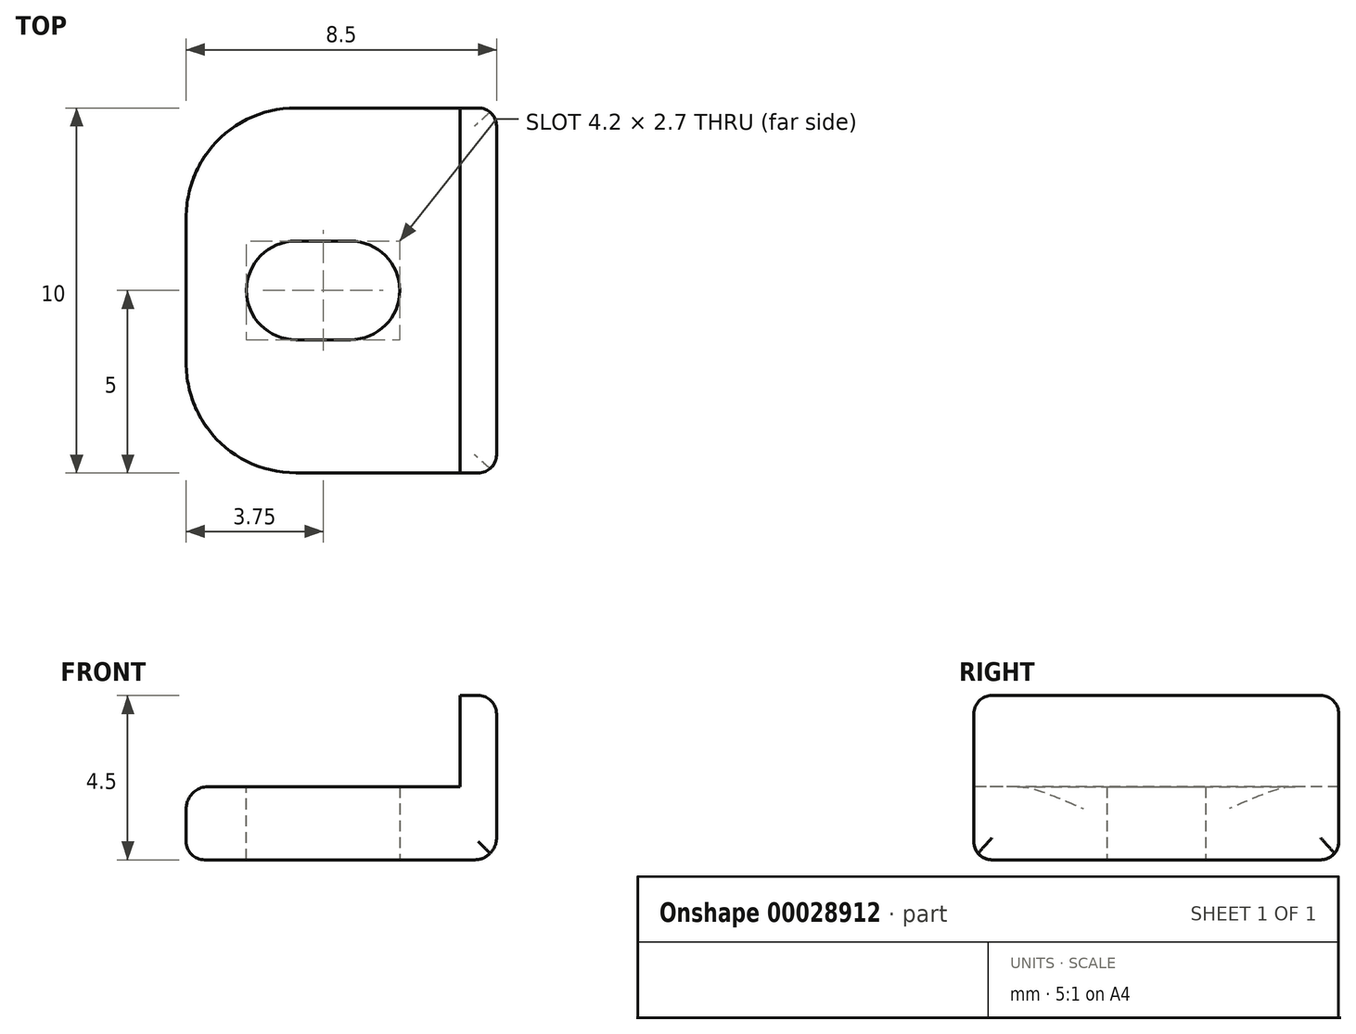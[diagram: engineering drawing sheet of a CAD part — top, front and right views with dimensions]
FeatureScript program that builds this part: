
annotation { "Feature Type Name" : "Feature", "Feature Type Description" : "" }
export const myFeature = defineFeature(function(context is Context, id is Id, definition is map)
    precondition{}
    {
        {
            var Q0;
            Q0=qCreatedBy(makeId("Top.planeOp"),FACE);
            var sketch = newSketch(context, id + "F0", { "sketchPlane" : qUnion([Q0])});
            skLineSegment(sketch, "E0.bottom", {"start": v(0, -10) * mm, "end": v(8.5, -10) * mm});
            skLineSegment(sketch, "E0.top", {"start": v(0, 0) * mm, "end": v(8.5, 0) * mm});
            skLineSegment(sketch, "E0.left", {"start": v(0, -10) * mm, "end": v(0, 0) * mm});
            skLineSegment(sketch, "E0.right", {"start": v(8.5, -10) * mm, "end": v(8.5, 0) * mm});
            skPoint(sketch, "E1", {"position": v(0, -5) * mm});
            skLineSegment(sketch, "E2", {"start": v(7.5, 0) * mm, "end": v(7.5, -10) * mm, "construction": true});
            skLineSegment(sketch, "E3", {"start": v(0, -5) * mm, "end": v(7.5, -5) * mm, "construction": true});
            skLineSegment(sketch, "E4.rect.bottom", {"start": v(5.85, -3.65) * mm, "end": v(1.65, -3.65) * mm});
            skLineSegment(sketch, "E4.rect.top", {"start": v(5.85, -6.35) * mm, "end": v(1.65, -6.35) * mm});
            skLineSegment(sketch, "E4.rect.left", {"start": v(5.85, -3.65) * mm, "end": v(5.85, -6.35) * mm});
            skLineSegment(sketch, "E4.rect.right", {"start": v(1.65, -3.65) * mm, "end": v(1.65, -6.35) * mm});
            skPoint(sketch, "E4.rect.middle", {"position": v(3.75, -5) * mm});
            skSolve(sketch);
        }
        {
            var Q0;
            Q0=makeQuery(id+"F0.imprint","IMPRINT",FACE,{"disambiguationData":[TD([[makeQuery(id+"F0.imprint","IMPRINT",EDGE,{"derivedFrom":sQuery(id+"F0.wireOp",EDGE,"E0.bottom")}),1.0]])]});
            extrude(context, id + "F1", {"entities" : qUnion([Q0]), "depth" : 2 * mm});
        }
        {
            var Q0;
            Q0=makeQuery(id+"F1.opExtrude","CAP_FACE",FACE,{"disambiguationData":[OSD([sQuery(id+"F0.wireOp",EDGE,"E0.bottom"),sQuery(id+"F0.wireOp",EDGE,"E0.top"),sQuery(id+"F0.wireOp",EDGE,"E0.left"),sQuery(id+"F0.wireOp",EDGE,"E0.right"),sQuery(id+"F0.wireOp",EDGE,"ae051ecd-3f90-4b7e-8cea-5822f81e962c")])],"isStart":false});
            var sketch = newSketch(context, id + "F2", { "sketchPlane" : qUnion([Q0])});
            skLineSegment(sketch, "E5", {"start": v(7.5, 0) * mm, "end": v(7.5, -10) * mm});
            skSolve(sketch);
        }
        {
            var Q0;
            {var subQ1=sQuery(id+"F2.wireOp",EDGE,"E5");Q0=makeQuery(id+"F2.imprint","IMPRINT",FACE,{"disambiguationData":[TD([[makeQuery(id+"F2.imprint","IMPRINT",EDGE,{"derivedFrom":subQ1}),1.0]])]});}
            extrude(context, id + "F3", {"entities" : qUnion([Q0]), "operationType" : NewBodyOperationType.ADD, "depth" : 2.5 * mm});
        }
        {
            var Q0;
            Q0=makeQuery(id+"F1.opExtrude","CAP_EDGE",EDGE,{"disambiguationData":[OSD([sQuery(id+"F0.wireOp",EDGE,"E0.bottom")])],"isStart":true});
            var Q1;
            {var subQ0=sQuery(id+"F0.wireOp",EDGE,"E0.bottom");var subQ1=sQuery(id+"F0.wireOp",EDGE,"E0.right");Q1=makeQuery(id+"F3.boolean.opBoolean","MERGE",EDGE,{"derivedFrom":[makeQuery(id+"F1.opExtrude","SWEPT_EDGE",EDGE,{"disambiguationData":[OSD([subQ0,subQ1])]}),makeQuery(id+"F3.opExtrude","SWEPT_EDGE",EDGE,{"disambiguationData":[OSD([subQ0,subQ1])]})]});}
            var Q2;
            {var subQ0=sQuery(id+"F0.wireOp",EDGE,"E0.top");var subQ1=sQuery(id+"F0.wireOp",EDGE,"E0.right");Q2=makeQuery(id+"F3.boolean.opBoolean","MERGE",EDGE,{"derivedFrom":[makeQuery(id+"F1.opExtrude","SWEPT_EDGE",EDGE,{"disambiguationData":[OSD([subQ0,subQ1])]}),makeQuery(id+"F3.opExtrude","SWEPT_EDGE",EDGE,{"disambiguationData":[OSD([subQ0,subQ1])]})]});}
            var Q3;
            Q3=makeQuery(id+"F1.opExtrude","CAP_EDGE",EDGE,{"disambiguationData":[OSD([sQuery(id+"F0.wireOp",EDGE,"E0.top")])],"isStart":true});
            var Q4;
            Q4=makeQuery(id+"F1.opExtrude","CAP_EDGE",EDGE,{"disambiguationData":[OSD([sQuery(id+"F0.wireOp",EDGE,"E0.left")])],"isStart":true});
            var Q5;
            Q5=makeQuery(id+"F3.opExtrude","CAP_EDGE",EDGE,{"disambiguationData":[OSD([sQuery(id+"F0.wireOp",EDGE,"E0.right")])],"isStart":false});
            var Q6;
            Q6=makeQuery(id+"F3.opExtrude","CAP_EDGE",EDGE,{"disambiguationData":[OSD([sQuery(id+"F0.wireOp",EDGE,"E0.bottom")])],"isStart":false});
            var Q7;
            Q7=makeQuery(id+"F3.opExtrude","CAP_EDGE",EDGE,{"disambiguationData":[OSD([sQuery(id+"F0.wireOp",EDGE,"E0.top")])],"isStart":false});
            var Q8;
            Q8=makeQuery(id+"F1.opExtrude","CAP_EDGE",EDGE,{"disambiguationData":[OSD([sQuery(id+"F0.wireOp",EDGE,"ae051ecd-3f90-4b7e-8cea-5822f81e962c")])],"isStart":false});
            var Q9;
            Q9=makeQuery(id+"F1.opExtrude","CAP_EDGE",EDGE,{"disambiguationData":[OSD([sQuery(id+"F0.wireOp",EDGE,"ae051ecd-3f90-4b7e-8cea-5822f81e962c")])],"isStart":true});
            fillet(context, id + "F4", {"entities" : qUnion([Q0, Q1, Q2, Q3, Q4, Q5, Q6, Q7, Q8, Q9]), "radius" : 0.5 * mm, "allowEdgeOverflow" : false});
        }
        {
            var Q0;
            Q0=makeQuery(id+"F1.opExtrude","SWEPT_EDGE",EDGE,{"disambiguationData":[OSD([sQuery(id+"F0.wireOp",EDGE,"E0.top"),sQuery(id+"F0.wireOp",EDGE,"E0.left")])]});
            var Q1;
            Q1=makeQuery(id+"F1.opExtrude","SWEPT_EDGE",EDGE,{"disambiguationData":[OSD([sQuery(id+"F0.wireOp",EDGE,"E0.bottom"),sQuery(id+"F0.wireOp",EDGE,"E0.left")])]});
            fillet(context, id + "F5", {"entities" : qUnion([Q0, Q1]), "radius" : 3 * mm, "tangentPropagation" : true, "allowEdgeOverflow" : false});
        }
        {
            var Q0;
            Q0=makeQuery(id+"F1.opExtrude","SWEPT_EDGE",EDGE,{"disambiguationData":[OSD([sQuery(id+"F0.wireOp",EDGE,"E4.rect.bottom"),sQuery(id+"F0.wireOp",EDGE,"E4.rect.right")])]});
            var Q1;
            Q1=makeQuery(id+"F1.opExtrude","SWEPT_EDGE",EDGE,{"disambiguationData":[OSD([sQuery(id+"F0.wireOp",EDGE,"E4.rect.bottom"),sQuery(id+"F0.wireOp",EDGE,"E4.rect.left")])]});
            var Q2;
            Q2=makeQuery(id+"F1.opExtrude","SWEPT_EDGE",EDGE,{"disambiguationData":[OSD([sQuery(id+"F0.wireOp",EDGE,"E4.rect.top"),sQuery(id+"F0.wireOp",EDGE,"E4.rect.left")])]});
            var Q3;
            Q3=makeQuery(id+"F1.opExtrude","SWEPT_EDGE",EDGE,{"disambiguationData":[OSD([sQuery(id+"F0.wireOp",EDGE,"E4.rect.top"),sQuery(id+"F0.wireOp",EDGE,"E4.rect.right")])]});
            fillet(context, id + "F6", {"entities" : qUnion([Q0, Q1, Q2, Q3]), "radius" : 1.35 * mm, "tangentPropagation" : true, "allowEdgeOverflow" : false});
        }
        {
            var Q0;
            Q0=makeQuery(id+"F1.opExtrude","CAP_EDGE",EDGE,{"disambiguationData":[OSD([sQuery(id+"F0.wireOp",EDGE,"E0.left")])],"isStart":false});
            var Q1;
            Q1=makeQuery(id+"F1.opExtrude","CAP_EDGE",EDGE,{"disambiguationData":[OSD([sQuery(id+"F0.wireOp",EDGE,"E0.right")])],"isStart":true});
            fillet(context, id + "F7", {"entities" : qUnion([Q0, Q1]), "radius" : 0.6 * mm, "allowEdgeOverflow" : false});
        }
    });
